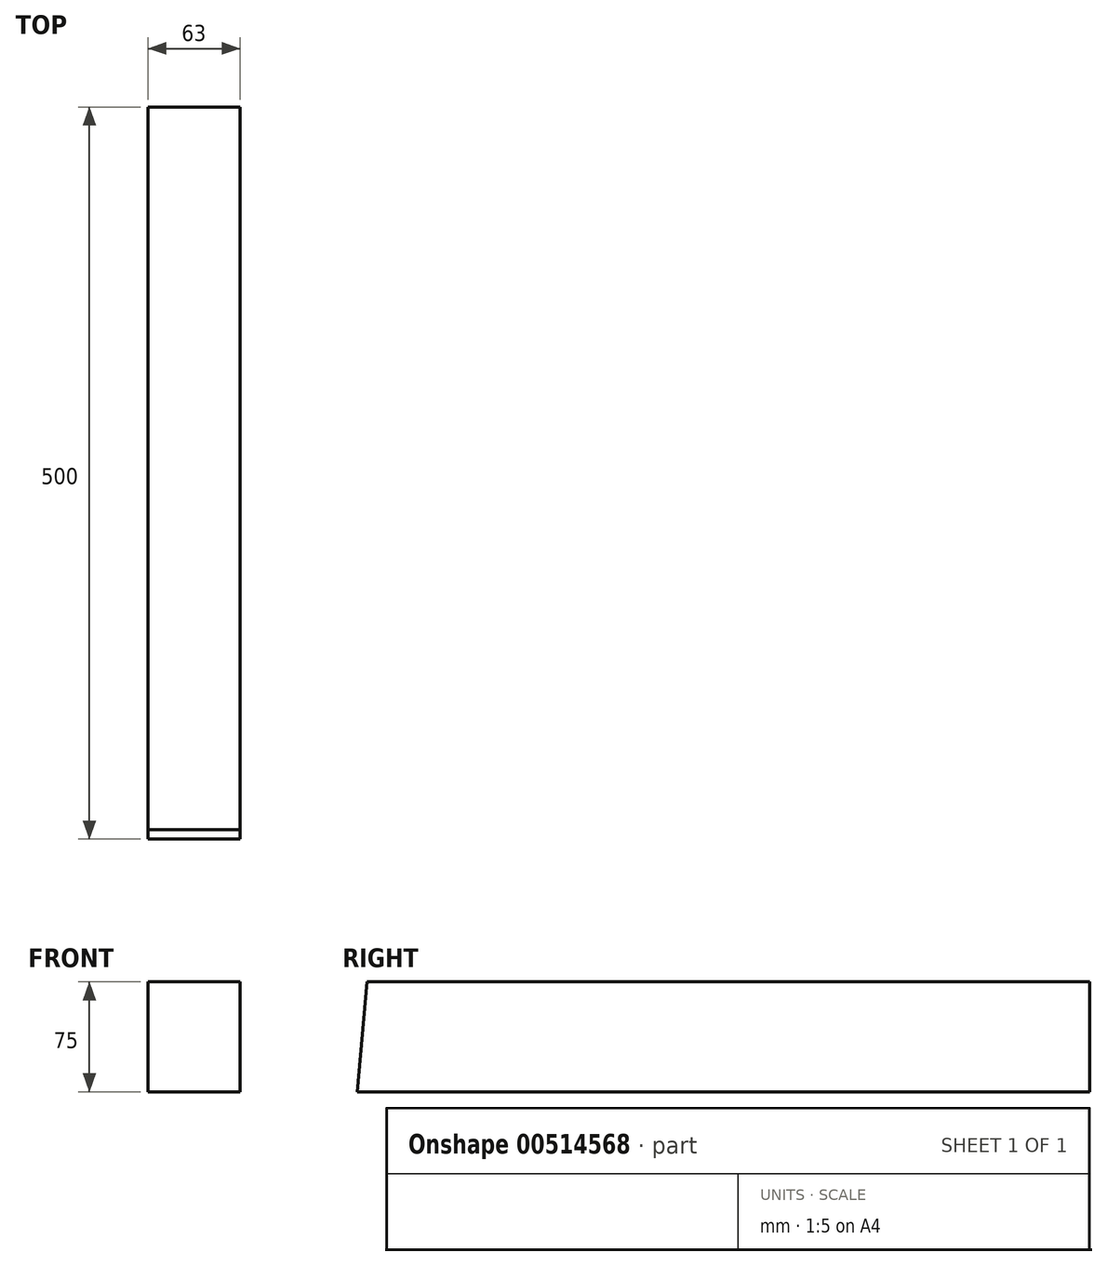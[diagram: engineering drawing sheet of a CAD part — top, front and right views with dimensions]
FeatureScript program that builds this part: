
annotation { "Feature Type Name" : "Feature", "Feature Type Description" : "" }
export const myFeature = defineFeature(function(context is Context, id is Id, definition is map)
    precondition{}
    {
        {
            var Q0;
            Q0=qCreatedBy(makeId("Front.planeOp"),FACE);
            var sketch = newSketch(context, id + "F0", { "sketchPlane" : qUnion([Q0])});
            skLineSegment(sketch, "E0.bottom", {"start": v(31.5, 37.5) * mm, "end": v(-31.5, 37.5) * mm});
            skLineSegment(sketch, "E0.top", {"start": v(31.5, -37.5) * mm, "end": v(-31.5, -37.5) * mm});
            skLineSegment(sketch, "E0.left", {"start": v(31.5, 37.5) * mm, "end": v(31.5, -37.5) * mm});
            skLineSegment(sketch, "E0.right", {"start": v(-31.5, 37.5) * mm, "end": v(-31.5, -37.5) * mm});
            skPoint(sketch, "E0.middle", {"position": v(0, 0) * mm});
            skSolve(sketch);
        }
        {
            var Q0;
            Q0=qSketchRegion(id+"F0",true);
            extrude(context, id + "F1", {"entities" : qUnion([Q0]), "depth" : 500 * mm});
        }
        {
            var Q0;
            Q0=makeQuery(id+"F1.opExtrude","SWEPT_FACE",FACE,{"disambiguationData":[OSD([sQuery(id+"F0.wireOp",EDGE,"E0.right")])]});
            var sketch = newSketch(context, id + "F2", { "sketchPlane" : qUnion([Q0])});
            skLineSegment(sketch, "E1", {"start": v(500, -37.5) * mm, "end": v(493.44, 37.5) * mm});
            skLineSegment(sketch, "E2", {"start": v(493.44, 37.5) * mm, "end": v(500, 37.5) * mm});
            skLineSegment(sketch, "E3", {"start": v(500, 37.5) * mm, "end": v(500, -37.5) * mm});
            skSolve(sketch);
        }
        {
            var Q0;
            Q0 = qSketchRegion(id + "F2", true);
            extrude(context, id + "F3", {"entities" : qUnion([Q0]), "operationType" : NewBodyOperationType.REMOVE, "endBound" : BoundingType.THROUGH_ALL, "oppositeDirection" : true, "depth" : 25 * mm});
        }
    });
